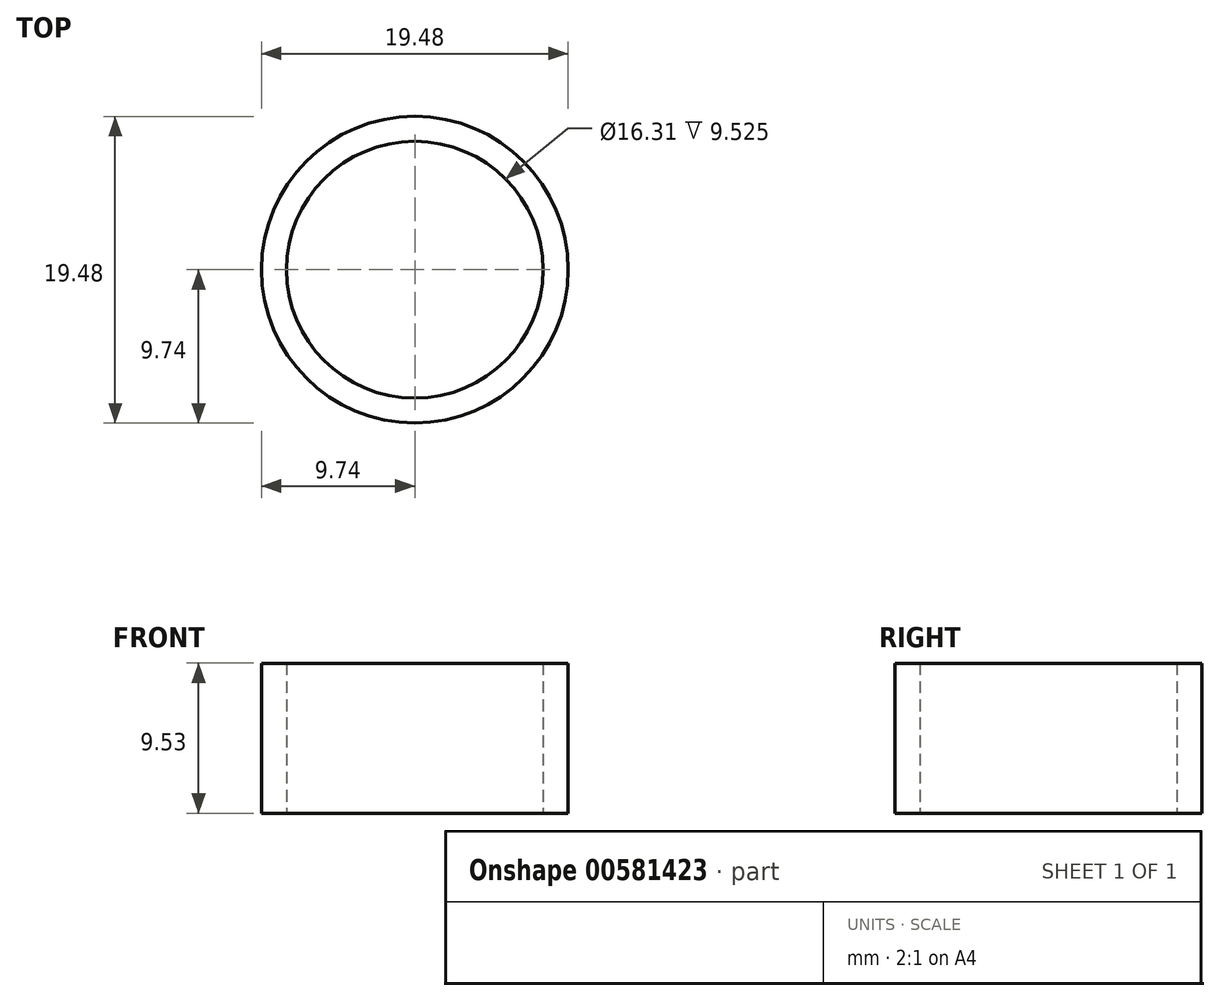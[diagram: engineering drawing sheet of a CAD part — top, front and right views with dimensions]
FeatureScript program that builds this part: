
annotation { "Feature Type Name" : "Feature", "Feature Type Description" : "" }
export const myFeature = defineFeature(function(context is Context, id is Id, definition is map)
    precondition{}
    {
        {
            var Q0;
            Q0=qCreatedBy(makeId("Top.planeOp"),FACE);
            var sketch = newSketch(context, id + "F0", { "sketchPlane" : qUnion([Q0])});
            skCircle(sketch, "E0", {"center": v(0, 0) * mm, "radius": 8.15 * mm});
            skCircle(sketch, "E1.0", {"center": v(0, 0) * mm, "radius": 9.74 * mm});
            skSolve(sketch);
        }
        {
            var Q0;
            Q0=makeQuery(id+"F0.imprint","IMPRINT",FACE,{"disambiguationData":[TD([[makeQuery(id+"F0.imprint","IMPRINT",EDGE,{"derivedFrom":sQuery(id+"F0.wireOp",EDGE,"E0")}),-1.0]])]});
            extrude(context, id + "F1", {"entities" : qUnion([Q0]), "depth" : 9.52 * mm, "offsetDistance" : 25.4 * mm});
        }
    });
